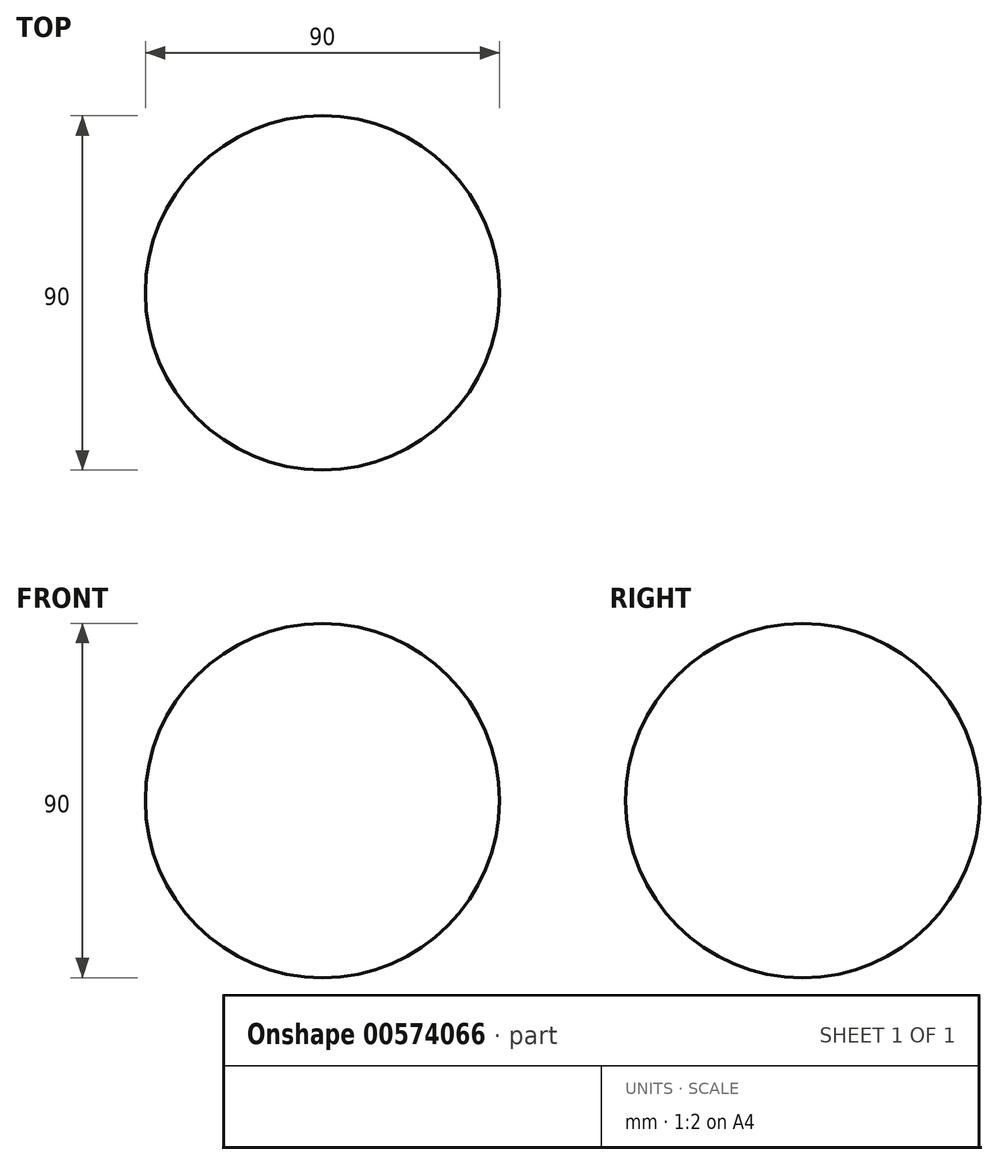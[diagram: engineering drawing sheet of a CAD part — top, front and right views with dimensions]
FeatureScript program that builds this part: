
annotation { "Feature Type Name" : "Feature", "Feature Type Description" : "" }
export const myFeature = defineFeature(function(context is Context, id is Id, definition is map)
    precondition{}
    {
        {
            var Q0;
            Q0=qCreatedBy(makeId("Top.planeOp"),FACE);
            var sketch = newSketch(context, id + "F0", { "sketchPlane" : qUnion([Q0])});
            skLineSegment(sketch, "E0", {"start": v(0, 45) * mm, "end": v(0, -45) * mm});
            skArc(sketch, "E1", {"start": v(45, 0) * mm, "mid": v(31.82, 31.82) * mm, "end": v(0, 45) * mm});
            skArc(sketch, "E2", {"start": v(45, 0) * mm, "mid": v(31.82, -31.82) * mm, "end": v(0, -45) * mm});
            skSolve(sketch);
        }
        {
            var Q0;
            Q0=makeQuery(id+"F0.imprint","IMPRINT",FACE,{"disambiguationData":[TD([[makeQuery(id+"F0.imprint","IMPRINT",EDGE,{"derivedFrom":sQuery(id+"F0.wireOp",EDGE,"E0")}),1.0]])]});
            var Q1;
            Q1=sQuery(id+"F0.wireOp",EDGE,"E0");
            revolve(context, id + "F1", {"entities" : qUnion([Q0]), "axis" : qUnion([Q1]), "revolveType" : RevolveType.SYMMETRIC, "angle" : 360 * degree});
        }
    });
